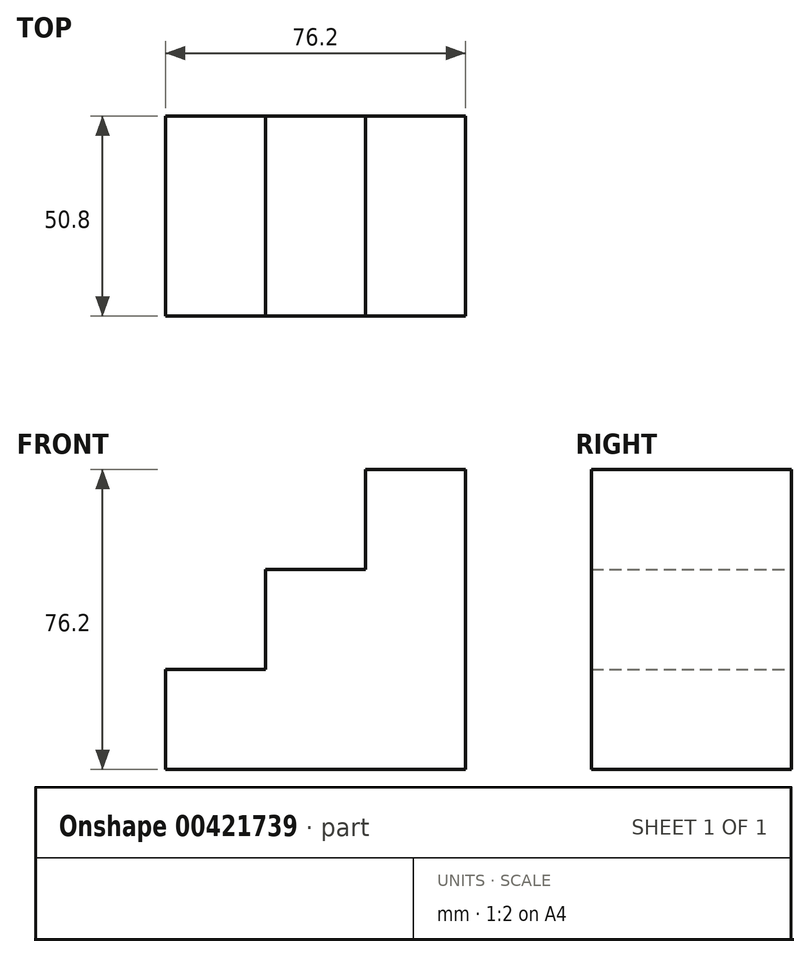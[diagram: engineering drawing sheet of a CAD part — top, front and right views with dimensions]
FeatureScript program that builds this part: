
annotation { "Feature Type Name" : "Feature", "Feature Type Description" : "" }
export const myFeature = defineFeature(function(context is Context, id is Id, definition is map)
    precondition{}
    {
        {
            var Q0;
            Q0=qCreatedBy(makeId("Front.planeOp"),FACE);
            var sketch = newSketch(context, id + "F0", { "sketchPlane" : qUnion([Q0])});
            skLineSegment(sketch, "E0", {"start": v(0, 0) * mm, "end": v(76.2, 0) * mm});
            skLineSegment(sketch, "E1", {"start": v(76.2, 0) * mm, "end": v(76.2, 76.2) * mm});
            skLineSegment(sketch, "E2", {"start": v(76.2, 76.2) * mm, "end": v(50.8, 76.2) * mm});
            skLineSegment(sketch, "E3", {"start": v(50.8, 76.2) * mm, "end": v(50.8, 50.8) * mm});
            skLineSegment(sketch, "E4", {"start": v(50.8, 50.8) * mm, "end": v(25.4, 50.8) * mm});
            skLineSegment(sketch, "E5", {"start": v(25.4, 50.8) * mm, "end": v(25.4, 25.4) * mm});
            skLineSegment(sketch, "E6", {"start": v(25.4, 25.4) * mm, "end": v(0, 25.4) * mm});
            skLineSegment(sketch, "E7", {"start": v(0, 25.4) * mm, "end": v(0, 0) * mm});
            skSolve(sketch);
        }
        {
            var Q0;
            Q0 = qSketchRegion(id + "F0", true);
            extrude(context, id + "F1", {"entities" : qUnion([Q0]), "depth" : 50.8 * mm});
        }
    });
